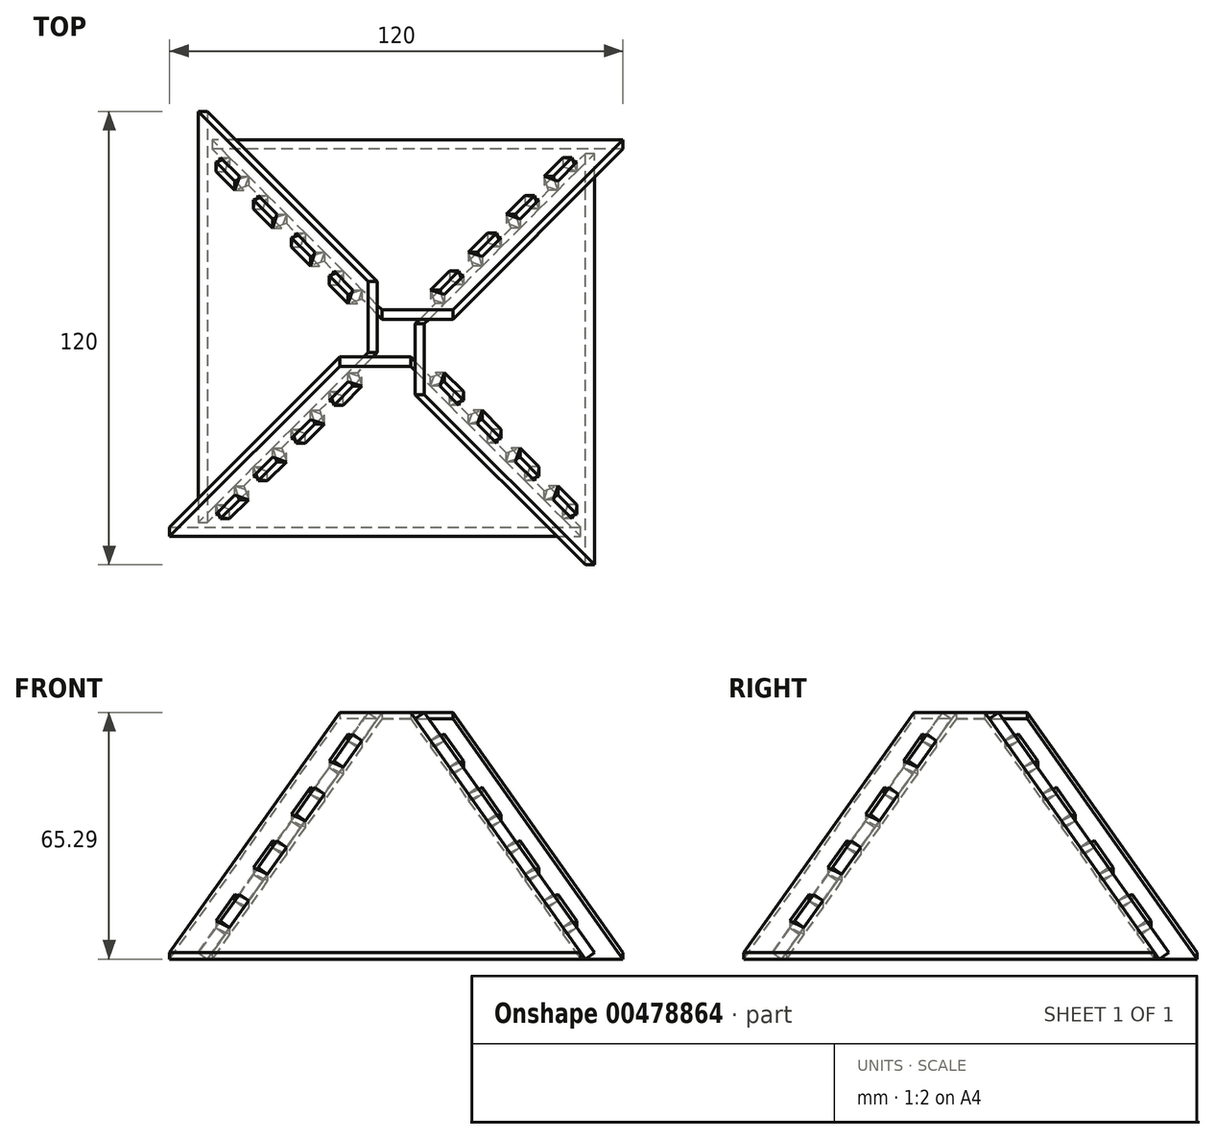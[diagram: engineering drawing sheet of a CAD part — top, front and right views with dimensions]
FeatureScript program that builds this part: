
annotation { "Feature Type Name" : "Feature", "Feature Type Description" : "" }
export const myFeature = defineFeature(function(context is Context, id is Id, definition is map)
    precondition{}
    {
        {
            var Q0;
            Q0=qCreatedBy(makeId("Top.planeOp"),FACE);
            var sketch = newSketch(context, id + "F0", { "sketchPlane" : qUnion([Q0])});
            skLineSegment(sketch, "E0.bottom", {"start": v(-50, 50) * mm, "end": v(50, 50) * mm});
            skLineSegment(sketch, "E0.top", {"start": v(-50, -50) * mm, "end": v(50, -50) * mm});
            skLineSegment(sketch, "E0.left", {"start": v(-50, 50) * mm, "end": v(-50, -50) * mm});
            skLineSegment(sketch, "E0.right", {"start": v(50, 50) * mm, "end": v(50, -50) * mm});
            skSolve(sketch);
        }
        {
            var Q0;
            Q0=qCreatedBy(makeId("Front.planeOp"),FACE);
            var sketch = newSketch(context, id + "F1", { "sketchPlane" : qUnion([Q0])});
            skLineSegment(sketch, "E1", {"start": v(0, 70.62) * mm, "end": v(0, 0) * mm});
            skLineSegment(sketch, "E2", {"start": v(0, 0) * mm, "end": v(50, 0) * mm});
            skLineSegment(sketch, "E3", {"start": v(50, 0) * mm, "end": v(0, 70.62) * mm});
            skLineSegment(sketch, "E4", {"start": v(0, 0) * mm, "end": v(33.3, 23.58) * mm});
            skSolve(sketch);
        }
        {
            var Q0;
            Q0=sQuery(id+"F1.wireOp",VERTEX,"E3.end");
            var Q1;
            Q1=sQuery(id+"F0.wireOp",VERTEX,"E0.right.end");
            var Q2;
            Q2=sQuery(id+"F0.wireOp",VERTEX,"E0.bottom.end");
            cPlane(context, id + "F2", {"entities" : qUnion([Q0, Q1, Q2]), "cplaneType" : CPlaneType.THREE_POINT, "offset" : 25 * mm, "width" : 150 * mm, "height" : 150 * mm});
        }
        {
            var Q0;
            Q0=qCreatedBy(id+"F2.planeOp",FACE);
            var sketch = newSketch(context, id + "F3", { "sketchPlane" : qUnion([Q0])});
            skLineSegment(sketch, "E5", {"start": v(-50, -28.9) * mm, "end": v(0, 57.63) * mm, "construction": true});
            skLineSegment(sketch, "E6", {"start": v(0, 57.63) * mm, "end": v(50, -28.9) * mm, "construction": true});
            skLineSegment(sketch, "E7", {"start": v(50, -28.9) * mm, "end": v(-50, -28.9) * mm, "construction": true});
            skLineSegment(sketch, "E8", {"start": v(0, -28.9) * mm, "end": v(0, 48.98) * mm});
            skLineSegment(sketch, "E9", {"start": v(0, 48.98) * mm, "end": v(-5, 48.98) * mm});
            skLineSegment(sketch, "E10", {"start": v(0, 48.98) * mm, "end": v(5, 48.98) * mm});
            skLineSegment(sketch, "E11", {"start": v(50, -28.9) * mm, "end": v(60, -28.9) * mm});
            skLineSegment(sketch, "E12", {"start": v(60, -28.9) * mm, "end": v(15, 48.98) * mm});
            skLineSegment(sketch, "E13.top", {"start": v(-12.76, 41.91) * mm, "end": v(-17.76, 33.26) * mm});
            skLineSegment(sketch, "E13.left", {"start": v(-10, 40.32) * mm, "end": v(-12.76, 41.91) * mm});
            skLineSegment(sketch, "E13.right", {"start": v(-15, 31.66) * mm, "end": v(-17.76, 33.26) * mm});
            skLineSegment(sketch, "E14.1.0.0", {"start": v(-20, 23) * mm, "end": v(-22.77, 24.6) * mm});
            skLineSegment(sketch, "E14.1.0.1", {"start": v(-22.77, 24.6) * mm, "end": v(-27.77, 15.94) * mm});
            skLineSegment(sketch, "E14.1.0.2", {"start": v(-25.01, 14.35) * mm, "end": v(-27.77, 15.94) * mm});
            skLineSegment(sketch, "E14.2.0.0", {"start": v(-30.02, 5.69) * mm, "end": v(-32.77, 7.28) * mm});
            skLineSegment(sketch, "E14.2.0.1", {"start": v(-32.77, 7.28) * mm, "end": v(-37.78, -1.38) * mm});
            skLineSegment(sketch, "E14.2.0.2", {"start": v(-35.02, -2.97) * mm, "end": v(-37.78, -1.38) * mm});
            skLineSegment(sketch, "E14.3.0.0", {"start": v(-40.02, -11.63) * mm, "end": v(-42.78, -10.04) * mm});
            skLineSegment(sketch, "E14.3.0.1", {"start": v(-42.78, -10.04) * mm, "end": v(-47.78, -18.7) * mm});
            skLineSegment(sketch, "E14.3.0.2", {"start": v(-45.03, -20.29) * mm, "end": v(-47.78, -18.7) * mm});
            skLineSegment(sketch, "E14.direction1", {"start": v(-10, 40.32) * mm, "end": v(-20, 23) * mm, "construction": true});
            skLineSegment(sketch, "E15", {"start": v(10, 40.32) * mm, "end": v(9.08, 39.8) * mm});
            skLineSegment(sketch, "E16", {"start": v(9.08, 39.8) * mm, "end": v(14.09, 31.13) * mm});
            skLineSegment(sketch, "E17", {"start": v(14.09, 31.13) * mm, "end": v(15, 31.66) * mm});
            skLineSegment(sketch, "E18", {"start": v(15, 31.66) * mm, "end": v(17.76, 33.26) * mm});
            skLineSegment(sketch, "E19", {"start": v(17.76, 33.26) * mm, "end": v(12.76, 41.91) * mm});
            skLineSegment(sketch, "E20", {"start": v(12.76, 41.91) * mm, "end": v(10, 40.32) * mm});
            skLineSegment(sketch, "E21", {"start": v(5, 48.98) * mm, "end": v(15, 48.98) * mm});
            skLineSegment(sketch, "E22.1.0.0", {"start": v(27.77, 15.94) * mm, "end": v(22.77, 24.6) * mm});
            skLineSegment(sketch, "E22.1.0.1", {"start": v(22.77, 24.6) * mm, "end": v(20, 23) * mm});
            skLineSegment(sketch, "E22.1.0.2", {"start": v(19.09, 22.47) * mm, "end": v(24.1, 13.82) * mm});
            skLineSegment(sketch, "E22.1.0.3", {"start": v(20, 23) * mm, "end": v(19.09, 22.47) * mm});
            skLineSegment(sketch, "E22.1.0.4", {"start": v(25.01, 14.35) * mm, "end": v(27.77, 15.94) * mm});
            skLineSegment(sketch, "E22.1.0.5", {"start": v(24.1, 13.82) * mm, "end": v(25.01, 14.35) * mm});
            skLineSegment(sketch, "E22.2.0.0", {"start": v(37.78, -1.38) * mm, "end": v(32.77, 7.28) * mm});
            skLineSegment(sketch, "E22.2.0.1", {"start": v(32.77, 7.28) * mm, "end": v(30.02, 5.69) * mm});
            skLineSegment(sketch, "E22.2.0.2", {"start": v(29.1, 5.16) * mm, "end": v(34.1, -3.5) * mm});
            skLineSegment(sketch, "E22.2.0.3", {"start": v(30.02, 5.69) * mm, "end": v(29.1, 5.16) * mm});
            skLineSegment(sketch, "E22.2.0.4", {"start": v(35.02, -2.97) * mm, "end": v(37.78, -1.38) * mm});
            skLineSegment(sketch, "E22.2.0.5", {"start": v(34.1, -3.5) * mm, "end": v(35.02, -2.97) * mm});
            skLineSegment(sketch, "E22.3.0.0", {"start": v(47.78, -18.7) * mm, "end": v(42.78, -10.04) * mm});
            skLineSegment(sketch, "E22.3.0.1", {"start": v(42.78, -10.04) * mm, "end": v(40.02, -11.63) * mm});
            skLineSegment(sketch, "E22.3.0.2", {"start": v(39.1, -12.16) * mm, "end": v(44.1, -20.82) * mm});
            skLineSegment(sketch, "E22.3.0.3", {"start": v(40.02, -11.63) * mm, "end": v(39.1, -12.16) * mm});
            skLineSegment(sketch, "E22.3.0.4", {"start": v(45.03, -20.29) * mm, "end": v(47.78, -18.7) * mm});
            skLineSegment(sketch, "E22.3.0.5", {"start": v(44.1, -20.82) * mm, "end": v(45.03, -20.29) * mm});
            skLineSegment(sketch, "E22.direction1", {"start": v(10, 40.32) * mm, "end": v(20, 23) * mm, "construction": true});
            skLineSegment(sketch, "E23", {"start": v(-3.77, 48.98) * mm, "end": v(-9.08, 39.8) * mm});
            skLineSegment(sketch, "E24", {"start": v(-9.08, 39.8) * mm, "end": v(-10, 40.32) * mm});
            skLineSegment(sketch, "E25", {"start": v(-15, 31.66) * mm, "end": v(-14.09, 31.13) * mm});
            skLineSegment(sketch, "E26", {"start": v(-14.09, 31.13) * mm, "end": v(-19.09, 22.47) * mm});
            skLineSegment(sketch, "E27", {"start": v(-19.09, 22.47) * mm, "end": v(-20, 23) * mm});
            skLineSegment(sketch, "E28.1.0.0", {"start": v(-25.01, 14.35) * mm, "end": v(-24.1, 13.82) * mm});
            skLineSegment(sketch, "E28.1.0.1", {"start": v(-24.1, 13.82) * mm, "end": v(-29.1, 5.16) * mm});
            skLineSegment(sketch, "E28.1.0.2", {"start": v(-29.1, 5.16) * mm, "end": v(-30.02, 5.69) * mm});
            skLineSegment(sketch, "E28.2.0.0", {"start": v(-35.02, -2.97) * mm, "end": v(-34.1, -3.5) * mm});
            skLineSegment(sketch, "E28.2.0.1", {"start": v(-34.1, -3.5) * mm, "end": v(-39.1, -12.16) * mm});
            skLineSegment(sketch, "E28.2.0.2", {"start": v(-39.1, -12.16) * mm, "end": v(-40.02, -11.63) * mm});
            skLineSegment(sketch, "E28.direction1", {"start": v(-20, 23) * mm, "end": v(-30.02, 5.69) * mm, "construction": true});
            skLineSegment(sketch, "E29.0.3.0", {"start": v(-45.03, -20.29) * mm, "end": v(-44.1, -20.82) * mm});
            skPoint(sketch, "E30.startSnap0", {"position": v(31.6, 0.83) * mm});
            skLineSegment(sketch, "E31", {"start": v(44.98, -2.9) * mm, "end": v(0, -28.9) * mm, "construction": true});
            skLineSegment(sketch, "E32", {"start": v(-37.48, -7.23) * mm, "end": v(0, -28.9) * mm, "construction": true});
            skLineSegment(sketch, "E33", {"start": v(-44.1, -20.82) * mm, "end": v(-48.77, -28.9) * mm});
            skLineSegment(sketch, "E34", {"start": v(50, -28.9) * mm, "end": v(-48.77, -28.9) * mm});
            skSolve(sketch);
        }
        {
            var Q0;
            {var subQ12=sQuery(id+"F3.wireOp",EDGE,"E11");Q0=makeQuery(id+"F3.imprint","IMPRINT",FACE,{"disambiguationData":[TD([[makeQuery(id+"F3.imprint","IMPRINT",EDGE,{"derivedFrom":subQ12}),1.0]])]});}
            var Q1;
            {var subQ5=sQuery(id+"F3.wireOp",EDGE,"E8");Q1=makeQuery(id+"F3.imprint","IMPRINT",FACE,{"disambiguationData":[TD([[makeQuery(id+"F3.imprint","IMPRINT",EDGE,{"derivedFrom":subQ5}),-1.0]])]});}
            var Q2;
            {var subQ12=sQuery(id+"F3.wireOp",EDGE,"E8");Q2=makeQuery(id+"F3.imprint","IMPRINT",FACE,{"disambiguationData":[TD([[makeQuery(id+"F3.imprint","IMPRINT",EDGE,{"derivedFrom":subQ12}),1.0]])]});}
            var Q3;
            Q3=makeQuery(id+"F3.imprint","IMPRINT",FACE,{"disambiguationData":[TD([[makeQuery(id+"F3.imprint","IMPRINT",EDGE,{"derivedFrom":sQuery(id+"F3.wireOp",EDGE,"E13.top")}),1.0]])]});
            var Q4;
            {var subQ0=sQuery(id+"F3.wireOp",EDGE,"E14.1.0.0");Q4=makeQuery(id+"F3.imprint","IMPRINT",FACE,{"disambiguationData":[TD([[makeQuery(id+"F3.imprint","IMPRINT",EDGE,{"derivedFrom":subQ0}),1.0]])]});}
            var Q5;
            {var subQ0=sQuery(id+"F3.wireOp",EDGE,"E14.2.0.0");Q5=makeQuery(id+"F3.imprint","IMPRINT",FACE,{"disambiguationData":[TD([[makeQuery(id+"F3.imprint","IMPRINT",EDGE,{"derivedFrom":subQ0}),1.0]])]});}
            var Q6;
            {var subQ0=sQuery(id+"F3.wireOp",EDGE,"E14.3.0.0");Q6=makeQuery(id+"F3.imprint","IMPRINT",FACE,{"disambiguationData":[TD([[makeQuery(id+"F3.imprint","IMPRINT",EDGE,{"derivedFrom":subQ0}),1.0]])]});}
            var Q7;
            {var subQ0=sQuery(id+"F3.wireOp",EDGE,"E14.4.0.0");Q7=makeQuery(id+"F3.imprint","IMPRINT",FACE,{"disambiguationData":[TD([[makeQuery(id+"F3.imprint","IMPRINT",EDGE,{"derivedFrom":subQ0}),1.0]])]});}
            extrude(context, id + "F4", {"entities" : qUnion([Q0, Q1, Q2, Q3, Q4, Q5, Q6, Q7]), "oppositeDirection" : true, "depth" : 3 * mm, "offsetDistance" : 25 * mm});
        }
        {
            var Q0;
            Q0=makeQuery(id+"F4.opExtrude","SWEPT_BODY",BODY,{"disambiguationData":[OSD([sQuery(id+"F3.wireOp",EDGE,"E5"),sQuery(id+"F3.wireOp",EDGE,"E7"),sQuery(id+"F3.wireOp",EDGE,"E9"),sQuery(id+"F3.wireOp",EDGE,"E10"),sQuery(id+"F3.wireOp",EDGE,"E11"),sQuery(id+"F3.wireOp",EDGE,"E12"),sQuery(id+"F3.wireOp",EDGE,"E13.top"),sQuery(id+"F3.wireOp",EDGE,"E13.left"),sQuery(id+"F3.wireOp",EDGE,"E13.right"),sQuery(id+"F3.wireOp",EDGE,"E14.1.0.0"),sQuery(id+"F3.wireOp",EDGE,"E14.1.0.1"),sQuery(id+"F3.wireOp",EDGE,"E14.1.0.2"),sQuery(id+"F3.wireOp",EDGE,"E14.2.0.0"),sQuery(id+"F3.wireOp",EDGE,"E14.2.0.1"),sQuery(id+"F3.wireOp",EDGE,"E14.2.0.2"),sQuery(id+"F3.wireOp",EDGE,"E14.3.0.0"),sQuery(id+"F3.wireOp",EDGE,"E14.3.0.1"),sQuery(id+"F3.wireOp",EDGE,"E14.3.0.2"),sQuery(id+"F3.wireOp",EDGE,"E14.4.0.0"),sQuery(id+"F3.wireOp",EDGE,"E14.4.0.1"),sQuery(id+"F3.wireOp",EDGE,"E14.4.0.2"),sQuery(id+"F3.wireOp",EDGE,"E15"),sQuery(id+"F3.wireOp",EDGE,"E16"),sQuery(id+"F3.wireOp",EDGE,"E17"),sQuery(id+"F3.wireOp",EDGE,"E18"),sQuery(id+"F3.wireOp",EDGE,"E19"),sQuery(id+"F3.wireOp",EDGE,"E20"),sQuery(id+"F3.wireOp",EDGE,"E21"),sQuery(id+"F3.wireOp",EDGE,"E22.1.0.0"),sQuery(id+"F3.wireOp",EDGE,"E22.1.0.1"),sQuery(id+"F3.wireOp",EDGE,"E22.1.0.2"),sQuery(id+"F3.wireOp",EDGE,"E22.1.0.3"),sQuery(id+"F3.wireOp",EDGE,"E22.1.0.4"),sQuery(id+"F3.wireOp",EDGE,"E22.1.0.5"),sQuery(id+"F3.wireOp",EDGE,"E22.2.0.0"),sQuery(id+"F3.wireOp",EDGE,"E22.2.0.1"),sQuery(id+"F3.wireOp",EDGE,"E22.2.0.2"),sQuery(id+"F3.wireOp",EDGE,"E22.2.0.3"),sQuery(id+"F3.wireOp",EDGE,"E22.2.0.4"),sQuery(id+"F3.wireOp",EDGE,"E22.2.0.5"),sQuery(id+"F3.wireOp",EDGE,"E22.3.0.0"),sQuery(id+"F3.wireOp",EDGE,"E22.3.0.1"),sQuery(id+"F3.wireOp",EDGE,"E22.3.0.2"),sQuery(id+"F3.wireOp",EDGE,"E22.3.0.3"),sQuery(id+"F3.wireOp",EDGE,"E22.3.0.4"),sQuery(id+"F3.wireOp",EDGE,"E22.3.0.5"),sQuery(id+"F3.wireOp",EDGE,"E22.4.0.0"),sQuery(id+"F3.wireOp",EDGE,"E22.4.0.1"),sQuery(id+"F3.wireOp",EDGE,"E22.4.0.2"),sQuery(id+"F3.wireOp",EDGE,"E22.4.0.3"),sQuery(id+"F3.wireOp",EDGE,"E22.4.0.4"),sQuery(id+"F3.wireOp",EDGE,"E22.4.0.5")])]});
            var Q1;
            Q1=makeQuery(id+"F4.opExtrude","SWEPT_BODY",BODY,{"disambiguationData":[OSD([sQuery(id+"F3.wireOp",EDGE,"E6"),sQuery(id+"F3.wireOp",EDGE,"E7"),sQuery(id+"F3.wireOp",EDGE,"E9"),sQuery(id+"F3.wireOp",EDGE,"E10"),sQuery(id+"F3.wireOp",EDGE,"E13.top"),sQuery(id+"F3.wireOp",EDGE,"E13.left"),sQuery(id+"F3.wireOp",EDGE,"E13.right"),sQuery(id+"F3.wireOp",EDGE,"E22.1.0.2"),sQuery(id+"F3.wireOp",EDGE,"E22.1.0.3"),sQuery(id+"F3.wireOp",EDGE,"E22.1.0.5"),sQuery(id+"F3.wireOp",EDGE,"E22.2.0.2"),sQuery(id+"F3.wireOp",EDGE,"E22.2.0.3"),sQuery(id+"F3.wireOp",EDGE,"E23"),sQuery(id+"F3.wireOp",EDGE,"E24"),sQuery(id+"F3.wireOp",EDGE,"E25"),sQuery(id+"F3.wireOp",EDGE,"E26"),sQuery(id+"F3.wireOp",EDGE,"E28.1.0.1"),sQuery(id+"F3.wireOp",EDGE,"E28.2.0.1"),sQuery(id+"F3.wireOp",EDGE,"DESngl6h-MrHg-kUYJ-6EBH-8XKota4PKjl1"),sQuery(id+"F3.wireOp",EDGE,"lwVZgezK-fTAP-kQ5W-Q0GH-lZDEmiM6u5cl"),sQuery(id+"F3.wireOp",EDGE,"yH9pOiUm-9FAw-OvBm-4Dhe-5Zgs9CQGBQb8")])]});
            var Q2;
            Q2=sQuery(id+"F1.wireOp",EDGE,"E1");
            circularPattern(context, id + "F5", {"entities" : qUnion([Q0, Q1]), "axis" : qUnion([Q2]), "angle" : 360 * degree, "instanceCount" : 4, "equalSpace" : true});
        }
        {
            var Q0;
            Q0=makeQuery(id+"F4.opExtrude","CAP_FACE",FACE,{"disambiguationData":[OSD([sQuery(id+"F3.wireOp",EDGE,"E7"),sQuery(id+"F3.wireOp",EDGE,"E9"),sQuery(id+"F3.wireOp",EDGE,"E10"),sQuery(id+"F3.wireOp",EDGE,"E11"),sQuery(id+"F3.wireOp",EDGE,"E12"),sQuery(id+"F3.wireOp",EDGE,"E13.top"),sQuery(id+"F3.wireOp",EDGE,"E13.left"),sQuery(id+"F3.wireOp",EDGE,"E13.right"),sQuery(id+"F3.wireOp",EDGE,"E14.1.0.0"),sQuery(id+"F3.wireOp",EDGE,"E14.1.0.1"),sQuery(id+"F3.wireOp",EDGE,"E14.1.0.2"),sQuery(id+"F3.wireOp",EDGE,"E14.2.0.0"),sQuery(id+"F3.wireOp",EDGE,"E14.2.0.1"),sQuery(id+"F3.wireOp",EDGE,"E14.2.0.2"),sQuery(id+"F3.wireOp",EDGE,"E14.3.0.0"),sQuery(id+"F3.wireOp",EDGE,"E14.3.0.1"),sQuery(id+"F3.wireOp",EDGE,"E14.3.0.2"),sQuery(id+"F3.wireOp",EDGE,"E14.4.0.0"),sQuery(id+"F3.wireOp",EDGE,"E14.4.0.1"),sQuery(id+"F3.wireOp",EDGE,"E14.4.0.2"),sQuery(id+"F3.wireOp",EDGE,"E15"),sQuery(id+"F3.wireOp",EDGE,"E16"),sQuery(id+"F3.wireOp",EDGE,"E17"),sQuery(id+"F3.wireOp",EDGE,"E18"),sQuery(id+"F3.wireOp",EDGE,"E19"),sQuery(id+"F3.wireOp",EDGE,"E20"),sQuery(id+"F3.wireOp",EDGE,"E21"),sQuery(id+"F3.wireOp",EDGE,"E22.1.0.0"),sQuery(id+"F3.wireOp",EDGE,"E22.1.0.1"),sQuery(id+"F3.wireOp",EDGE,"E22.1.0.2"),sQuery(id+"F3.wireOp",EDGE,"E22.1.0.3"),sQuery(id+"F3.wireOp",EDGE,"E22.1.0.4"),sQuery(id+"F3.wireOp",EDGE,"E22.1.0.5"),sQuery(id+"F3.wireOp",EDGE,"E22.2.0.0"),sQuery(id+"F3.wireOp",EDGE,"E22.2.0.1"),sQuery(id+"F3.wireOp",EDGE,"E22.2.0.2"),sQuery(id+"F3.wireOp",EDGE,"E22.2.0.3"),sQuery(id+"F3.wireOp",EDGE,"E22.2.0.4"),sQuery(id+"F3.wireOp",EDGE,"E22.2.0.5"),sQuery(id+"F3.wireOp",EDGE,"E22.3.0.0"),sQuery(id+"F3.wireOp",EDGE,"E22.3.0.1"),sQuery(id+"F3.wireOp",EDGE,"E22.3.0.2"),sQuery(id+"F3.wireOp",EDGE,"E22.3.0.3"),sQuery(id+"F3.wireOp",EDGE,"E22.3.0.4"),sQuery(id+"F3.wireOp",EDGE,"E22.3.0.5"),sQuery(id+"F3.wireOp",EDGE,"E22.4.0.0"),sQuery(id+"F3.wireOp",EDGE,"E22.4.0.1"),sQuery(id+"F3.wireOp",EDGE,"E22.4.0.2"),sQuery(id+"F3.wireOp",EDGE,"E22.4.0.3"),sQuery(id+"F3.wireOp",EDGE,"E22.4.0.4"),sQuery(id+"F3.wireOp",EDGE,"E22.4.0.5"),sQuery(id+"F3.wireOp",EDGE,"E23"),sQuery(id+"F3.wireOp",EDGE,"E24"),sQuery(id+"F3.wireOp",EDGE,"E25"),sQuery(id+"F3.wireOp",EDGE,"E26"),sQuery(id+"F3.wireOp",EDGE,"E27"),sQuery(id+"F3.wireOp",EDGE,"E28.1.0.0"),sQuery(id+"F3.wireOp",EDGE,"E28.1.0.1"),sQuery(id+"F3.wireOp",EDGE,"E28.1.0.2"),sQuery(id+"F3.wireOp",EDGE,"E28.2.0.0"),sQuery(id+"F3.wireOp",EDGE,"E28.2.0.1"),sQuery(id+"F3.wireOp",EDGE,"E28.2.0.2"),sQuery(id+"F3.wireOp",EDGE,"E29.0.3.0"),sQuery(id+"F3.wireOp",EDGE,"E29.3.3.0"),sQuery(id+"F3.wireOp",EDGE,"E29.6.3.0"),sQuery(id+"F3.wireOp",EDGE,"0MXYEX2e-yWjQ-y4ph-eJsH-lQV5XsRj777Y"),sQuery(id+"F3.wireOp",EDGE,"bN6kEwG8-yHYI-711u-lRRn-Bhmo0L1RSKKt")])],"isStart":false});
            var sketch = newSketch(context, id + "F6", { "sketchPlane" : qUnion([Q0])});
            skPoint(sketch, "E35", {"position": v(0, -28.9) * mm});
            skLineSegment(sketch, "E36", {"start": v(0, -28.9) * mm, "end": v(40.24, -5.64) * mm});
            skSolve(sketch);
        }
        {
            var Q0;
            Q0=makeQuery(id+"F5.opPattern","COPY",FACE,{"derivedFrom":makeQuery(id+"F4.opExtrude","CAP_FACE",FACE,{"disambiguationData":[OSD([sQuery(id+"F3.wireOp",EDGE,"E7"),sQuery(id+"F3.wireOp",EDGE,"E9"),sQuery(id+"F3.wireOp",EDGE,"E10"),sQuery(id+"F3.wireOp",EDGE,"E11"),sQuery(id+"F3.wireOp",EDGE,"E12"),sQuery(id+"F3.wireOp",EDGE,"E13.top"),sQuery(id+"F3.wireOp",EDGE,"E13.left"),sQuery(id+"F3.wireOp",EDGE,"E13.right"),sQuery(id+"F3.wireOp",EDGE,"E14.1.0.0"),sQuery(id+"F3.wireOp",EDGE,"E14.1.0.1"),sQuery(id+"F3.wireOp",EDGE,"E14.1.0.2"),sQuery(id+"F3.wireOp",EDGE,"E14.2.0.0"),sQuery(id+"F3.wireOp",EDGE,"E14.2.0.1"),sQuery(id+"F3.wireOp",EDGE,"E14.2.0.2"),sQuery(id+"F3.wireOp",EDGE,"E14.3.0.0"),sQuery(id+"F3.wireOp",EDGE,"E14.3.0.1"),sQuery(id+"F3.wireOp",EDGE,"E14.3.0.2"),sQuery(id+"F3.wireOp",EDGE,"E14.4.0.0"),sQuery(id+"F3.wireOp",EDGE,"E14.4.0.1"),sQuery(id+"F3.wireOp",EDGE,"E14.4.0.2"),sQuery(id+"F3.wireOp",EDGE,"E15"),sQuery(id+"F3.wireOp",EDGE,"E16"),sQuery(id+"F3.wireOp",EDGE,"E17"),sQuery(id+"F3.wireOp",EDGE,"E18"),sQuery(id+"F3.wireOp",EDGE,"E19"),sQuery(id+"F3.wireOp",EDGE,"E20"),sQuery(id+"F3.wireOp",EDGE,"E21"),sQuery(id+"F3.wireOp",EDGE,"E22.1.0.0"),sQuery(id+"F3.wireOp",EDGE,"E22.1.0.1"),sQuery(id+"F3.wireOp",EDGE,"E22.1.0.2"),sQuery(id+"F3.wireOp",EDGE,"E22.1.0.3"),sQuery(id+"F3.wireOp",EDGE,"E22.1.0.4"),sQuery(id+"F3.wireOp",EDGE,"E22.1.0.5"),sQuery(id+"F3.wireOp",EDGE,"E22.2.0.0"),sQuery(id+"F3.wireOp",EDGE,"E22.2.0.1"),sQuery(id+"F3.wireOp",EDGE,"E22.2.0.2"),sQuery(id+"F3.wireOp",EDGE,"E22.2.0.3"),sQuery(id+"F3.wireOp",EDGE,"E22.2.0.4"),sQuery(id+"F3.wireOp",EDGE,"E22.2.0.5"),sQuery(id+"F3.wireOp",EDGE,"E22.3.0.0"),sQuery(id+"F3.wireOp",EDGE,"E22.3.0.1"),sQuery(id+"F3.wireOp",EDGE,"E22.3.0.2"),sQuery(id+"F3.wireOp",EDGE,"E22.3.0.3"),sQuery(id+"F3.wireOp",EDGE,"E22.3.0.4"),sQuery(id+"F3.wireOp",EDGE,"E22.3.0.5"),sQuery(id+"F3.wireOp",EDGE,"E22.4.0.0"),sQuery(id+"F3.wireOp",EDGE,"E22.4.0.1"),sQuery(id+"F3.wireOp",EDGE,"E22.4.0.2"),sQuery(id+"F3.wireOp",EDGE,"E22.4.0.3"),sQuery(id+"F3.wireOp",EDGE,"E22.4.0.4"),sQuery(id+"F3.wireOp",EDGE,"E22.4.0.5"),sQuery(id+"F3.wireOp",EDGE,"E23"),sQuery(id+"F3.wireOp",EDGE,"E24"),sQuery(id+"F3.wireOp",EDGE,"E25"),sQuery(id+"F3.wireOp",EDGE,"E26"),sQuery(id+"F3.wireOp",EDGE,"E27"),sQuery(id+"F3.wireOp",EDGE,"E28.1.0.0"),sQuery(id+"F3.wireOp",EDGE,"E28.1.0.1"),sQuery(id+"F3.wireOp",EDGE,"E28.1.0.2"),sQuery(id+"F3.wireOp",EDGE,"E28.2.0.0"),sQuery(id+"F3.wireOp",EDGE,"E28.2.0.1"),sQuery(id+"F3.wireOp",EDGE,"E28.2.0.2"),sQuery(id+"F3.wireOp",EDGE,"E29.0.3.0"),sQuery(id+"F3.wireOp",EDGE,"E29.3.3.0"),sQuery(id+"F3.wireOp",EDGE,"E29.6.3.0"),sQuery(id+"F3.wireOp",EDGE,"0MXYEX2e-yWjQ-y4ph-eJsH-lQV5XsRj777Y"),sQuery(id+"F3.wireOp",EDGE,"bN6kEwG8-yHYI-711u-lRRn-Bhmo0L1RSKKt")])],"isStart":false}),"instanceName":"3"});
            var sketch = newSketch(context, id + "F7", { "sketchPlane" : qUnion([Q0])});
            skPoint(sketch, "E37", {"position": v(0, -28.9) * mm});
            skLineSegment(sketch, "E38", {"start": v(0, -28.9) * mm, "end": v(-44.98, -2.9) * mm});
            skSolve(sketch);
        }
        {
            var Q0;
            Q0=sQuery(id+"F7.wireOp",VERTEX,"E37");
            var Q1;
            Q1=sQuery(id+"F7.wireOp",VERTEX,"E38.end");
            var Q2;
            Q2=sQuery(id+"F6.wireOp",VERTEX,"E35");
            cPlane(context, id + "F8", {"entities" : qUnion([Q0, Q1, Q2]), "cplaneType" : CPlaneType.THREE_POINT, "offset" : 25 * mm, "width" : 150 * mm, "height" : 150 * mm});
        }
    });
